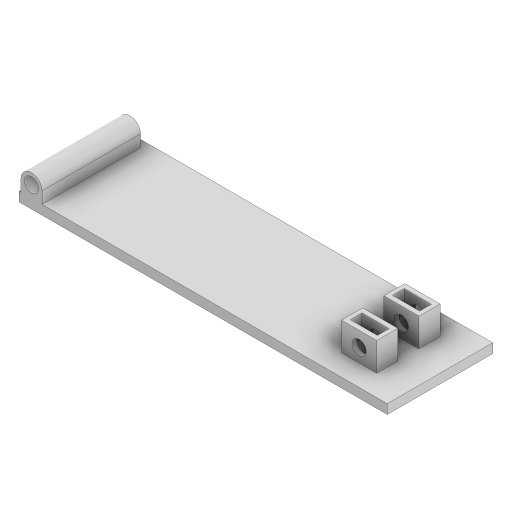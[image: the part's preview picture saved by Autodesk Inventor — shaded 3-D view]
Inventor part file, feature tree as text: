
AUTODESK INVENTOR PART (.ipt)
format: ipt  version: 2023.3 (Build 273359000, 359)  size: 220,160 bytes
history: native  units: mm
features: sketch x6, extrude x5, plane x1, mirror x1, projected_geometry x1
ambient origin geometry x8: Origin, YZ Plane, XZ Plane, XY Plane, X Axis, Y Axis, Z Axis, Center Point
bodies: Solid1 (feature_tree)
feature tree (14):
  extrude  "Extrusion1"  Depth=78.5mm
  extrude  "Extrusion2"  Depth=22.5mm
  extrude  "Extrusion3"  Depth=3.0mm
  extrude  "Extrusion4"  Depth=4.5mm
  plane  "Work Plane1"
  mirror  "Mirror1"
  sketch  "Sketch5"  dims[d9=10.5mm d10=3.0mm]
  extrude  "Extrusion5"  Depth=3.0mm
  sketch  "Sketch1"  dims[d0=2.0mm d1=78.5mm]
  sketch  "Sketch2"  dims[d2=22.5mm d3=0.0mm d4=2.62mm]
  sketch  "Sketch3"  dims[d5=2.5mm d6=3.0mm]
  sketch  "Sketch4"  dims[d7=4.5mm d8=2.875mm]
  projected_geometry  "Projected Loop1"
  sketch  "Sketch6"  dims[d11=4.5mm d12=5.5mm d13=7.5mm d14=0.0mm d15=4.5mm d16=4.5mm d17=4.5mm d18=4.5mm d19=22.5mm d20=0.0mm d21=5.8mm d22=2.5mm d23=5.8mm d24=2.5mm d25=6.351mm d26=0.0mm d27=6.351mm d28=0.0mm d29=2.25mm d30=1.5mm d31=10.0mm d32=0.0mm]
